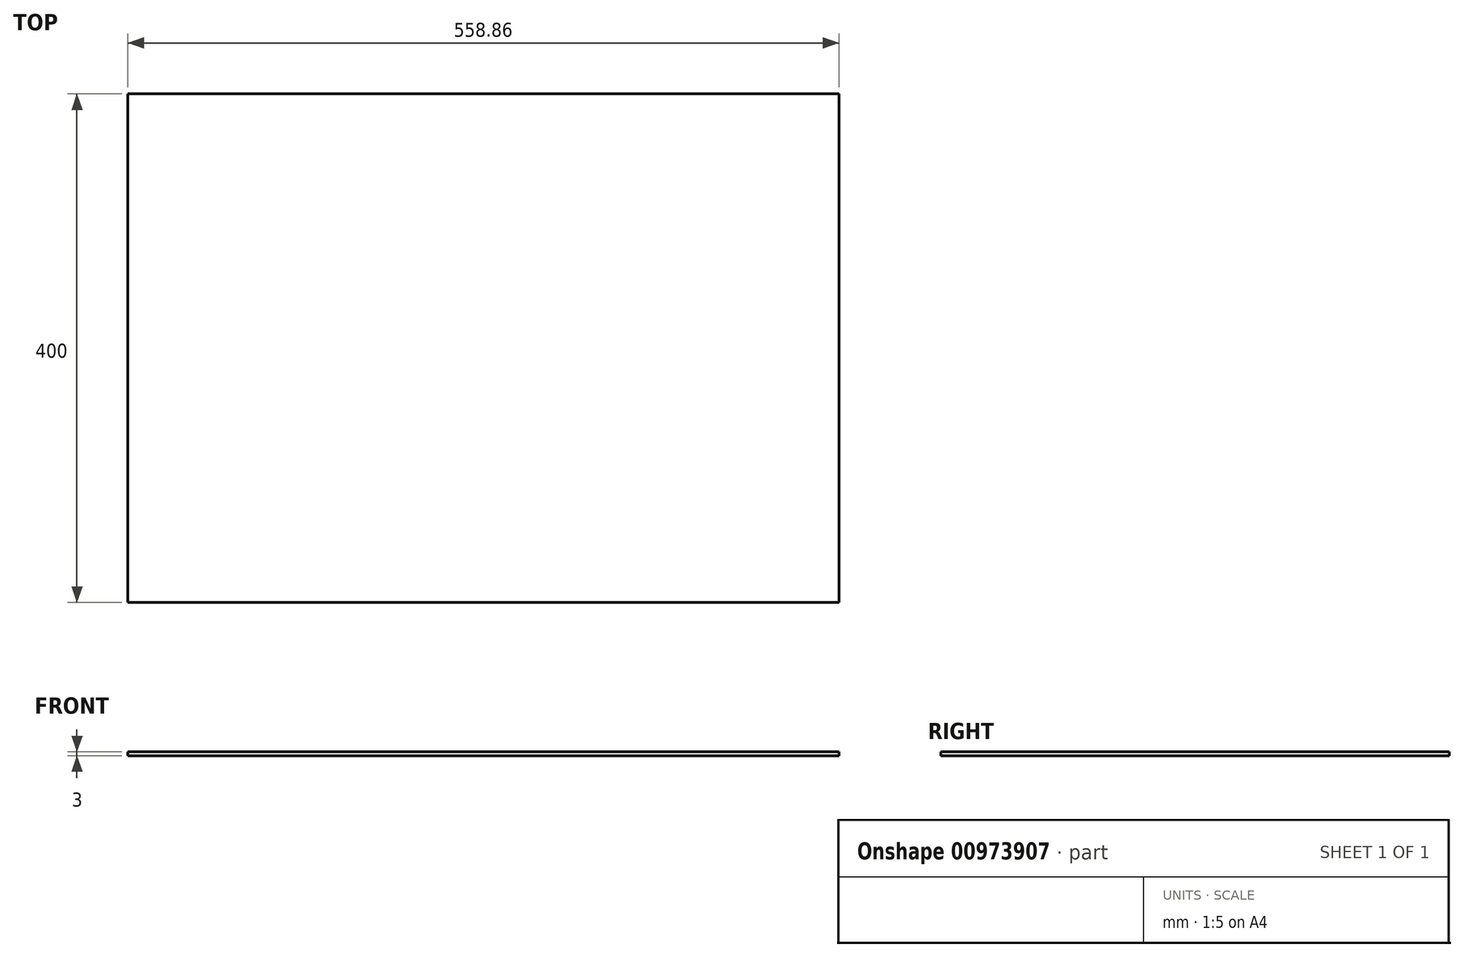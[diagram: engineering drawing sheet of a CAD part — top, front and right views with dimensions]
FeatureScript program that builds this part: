
annotation { "Feature Type Name" : "Feature", "Feature Type Description" : "" }
export const myFeature = defineFeature(function(context is Context, id is Id, definition is map)
    precondition{}
    {
        {
            var Q0;
            Q0=qCreatedBy(makeId("Top.planeOp"),FACE);
            var sketch = newSketch(context, id + "F0", { "sketchPlane" : qUnion([Q0])});
            skLineSegment(sketch, "E0.bottom", {"start": v(279.43, 200) * mm, "end": v(-279.43, 200) * mm});
            skLineSegment(sketch, "E0.top", {"start": v(279.43, -200) * mm, "end": v(-279.43, -200) * mm});
            skLineSegment(sketch, "E0.left", {"start": v(279.43, 200) * mm, "end": v(279.43, -200) * mm});
            skLineSegment(sketch, "E0.right", {"start": v(-279.43, 200) * mm, "end": v(-279.43, -200) * mm});
            skPoint(sketch, "E0.middle", {"position": v(0, 0) * mm});
            skSolve(sketch);
        }
        {
            var Q0;
            Q0=makeQuery(id+"F0.imprint","IMPRINT",FACE,{"disambiguationData":[TD([[makeQuery(id+"F0.imprint","IMPRINT",EDGE,{"derivedFrom":sQuery(id+"F0.wireOp",EDGE,"E0.bottom")}),1.0]])]});
            var sketch = newSketch(context, id + "F1", { "sketchPlane" : qUnion([Q0])});
            skSolve(sketch);
        }
        {
            var Q0;
            Q0=makeQuery(id+"F1.imprint","IMPRINT",FACE,{"disambiguationData":[TD([[makeQuery(id+"F1.imprint","IMPRINT",EDGE,{"derivedFrom":makeQuery(id+"F0.imprint","IMPRINT",EDGE,{"derivedFrom":sQuery(id+"F0.wireOp",EDGE,"E0.bottom")})}),1.0]])]});
            extrude(context, id + "F2", {"entities" : qUnion([Q0]), "depth" : 3 * mm, "offsetDistance" : 25 * mm});
        }
    });
